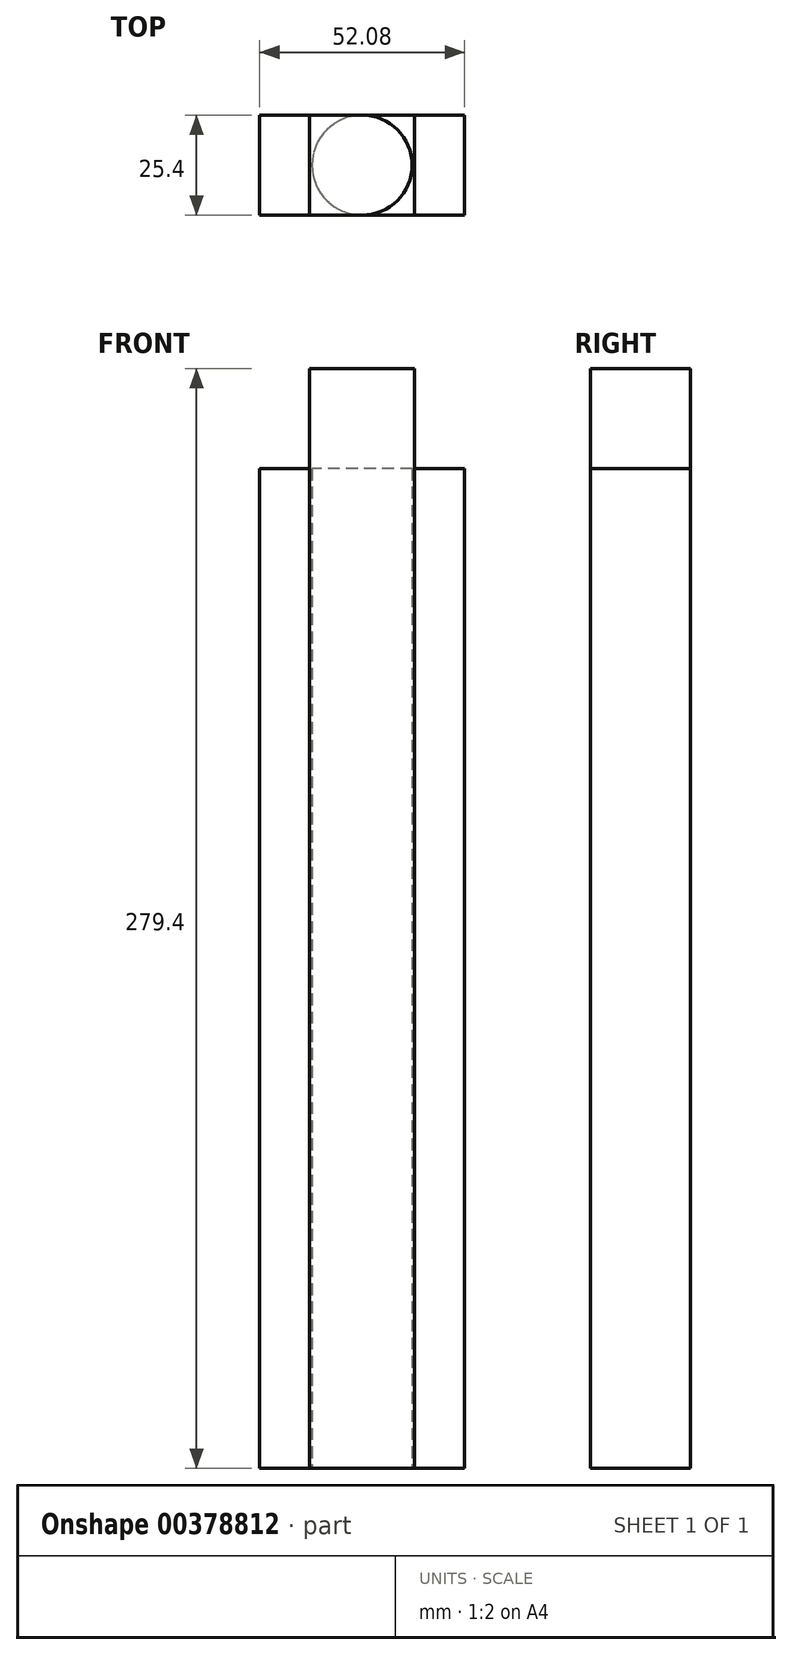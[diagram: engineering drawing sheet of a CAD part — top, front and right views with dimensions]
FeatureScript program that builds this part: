
annotation { "Feature Type Name" : "Feature", "Feature Type Description" : "" }
export const myFeature = defineFeature(function(context is Context, id is Id, definition is map)
    precondition{}
    {
        {
            var Q0;
            Q0=qCreatedBy(makeId("Top.planeOp"),FACE);
            var sketch = newSketch(context, id + "F0", { "sketchPlane" : qUnion([Q0])});
            skCircle(sketch, "E0", {"center": v(0, 0) * mm, "radius": 12.7 * mm});
            skSolve(sketch);
        }
        {
            var Q0;
            Q0=makeQuery(id+"F0.imprint","IMPRINT",FACE,{"disambiguationData":[TD([[makeQuery(id+"F0.imprint","IMPRINT",EDGE,{"derivedFrom":sQuery(id+"F0.wireOp",EDGE,"E0")}),1.0]])]});
            extrude(context, id + "F1", {"entities" : qUnion([Q0]), "depth" : 254 * mm});
        }
        {
            var Q0;
            Q0=qCreatedBy(makeId("Top.planeOp"),FACE);
            var sketch = newSketch(context, id + "F2", { "sketchPlane" : qUnion([Q0])});
            skLineSegment(sketch, "E1.bottom", {"start": v(9.53, -7.94) * mm, "end": v(-9.53, -7.94) * mm});
            skLineSegment(sketch, "E1.top", {"start": v(9.53, 7.94) * mm, "end": v(-9.53, 7.94) * mm});
            skLineSegment(sketch, "E1.left", {"start": v(9.53, -7.94) * mm, "end": v(9.53, 7.94) * mm});
            skLineSegment(sketch, "E1.right", {"start": v(-9.53, -7.94) * mm, "end": v(-9.53, 7.94) * mm});
            skPoint(sketch, "E1.middle", {"position": v(0, 0) * mm});
            skLineSegment(sketch, "E2.bottom", {"start": v(-13.33, 12.7) * mm, "end": v(13.34, 12.7) * mm});
            skLineSegment(sketch, "E2.top", {"start": v(-13.33, 3.18) * mm, "end": v(13.34, 3.18) * mm});
            skLineSegment(sketch, "E2.left", {"start": v(-13.33, 12.7) * mm, "end": v(-13.33, 3.18) * mm});
            skLineSegment(sketch, "E2.right", {"start": v(13.34, 12.7) * mm, "end": v(13.34, 3.18) * mm});
            skPoint(sketch, "E2.middle", {"position": v(0, 7.94) * mm});
            skLineSegment(sketch, "E3", {"start": v(-22.62, 0) * mm, "end": v(27.7, 0) * mm, "construction": true});
            skLineSegment(sketch, "E4.MirrorCS", {"start": v(-13.33, -12.7) * mm, "end": v(13.34, -12.7) * mm});
            skLineSegment(sketch, "E5.MirrorCS", {"start": v(-13.33, -12.7) * mm, "end": v(-13.33, -3.18) * mm});
            skLineSegment(sketch, "E6.MirrorCS", {"start": v(-13.33, -3.18) * mm, "end": v(13.34, -3.18) * mm});
            skLineSegment(sketch, "E7.MirrorCS", {"start": v(13.34, -12.7) * mm, "end": v(13.34, -3.18) * mm});
            skLineSegment(sketch, "E8.bottom", {"start": v(-13.33, 12.7) * mm, "end": v(-26.04, 12.7) * mm});
            skLineSegment(sketch, "E8.top", {"start": v(-13.33, -12.7) * mm, "end": v(-26.04, -12.7) * mm});
            skLineSegment(sketch, "E8.left", {"start": v(-13.33, 12.7) * mm, "end": v(-13.33, -12.7) * mm});
            skLineSegment(sketch, "E8.right", {"start": v(-26.04, 12.7) * mm, "end": v(-26.04, -12.7) * mm});
            skLineSegment(sketch, "E9.bottom", {"start": v(-9.52, -3.18) * mm, "end": v(-13.33, -3.18) * mm});
            skLineSegment(sketch, "E9.top", {"start": v(-9.52, 3.18) * mm, "end": v(-13.33, 3.18) * mm});
            skLineSegment(sketch, "E9.left", {"start": v(-9.53, -3.18) * mm, "end": v(-9.52, 3.18) * mm});
            skLineSegment(sketch, "E9.right", {"start": v(-13.33, -3.18) * mm, "end": v(-13.33, 3.18) * mm});
            skLineSegment(sketch, "E10", {"start": v(0, 20.94) * mm, "end": v(0, -20) * mm, "construction": true});
            skLineSegment(sketch, "E11.MirrorCS", {"start": v(13.33, -3.18) * mm, "end": v(13.33, 3.18) * mm});
            skLineSegment(sketch, "E12.MirrorCS", {"start": v(9.53, -3.18) * mm, "end": v(9.53, 3.18) * mm});
            skLineSegment(sketch, "E13.MirrorCS", {"start": v(13.33, -12.7) * mm, "end": v(13.33, -3.18) * mm});
            skLineSegment(sketch, "E14.MirrorCS", {"start": v(9.52, 3.18) * mm, "end": v(13.33, 3.18) * mm});
            skLineSegment(sketch, "E15.MirrorCS", {"start": v(13.33, -12.7) * mm, "end": v(26.04, -12.7) * mm});
            skLineSegment(sketch, "E16.MirrorCS", {"start": v(13.33, 12.7) * mm, "end": v(13.33, 3.18) * mm});
            skLineSegment(sketch, "E17.MirrorCS", {"start": v(13.33, 12.7) * mm, "end": v(26.04, 12.7) * mm});
            skLineSegment(sketch, "E18.MirrorCS", {"start": v(13.33, 12.7) * mm, "end": v(13.33, -12.7) * mm});
            skLineSegment(sketch, "E19.MirrorCS", {"start": v(9.52, -3.18) * mm, "end": v(13.33, -3.18) * mm});
            skLineSegment(sketch, "E20.MirrorCS", {"start": v(26.04, 12.7) * mm, "end": v(26.04, -12.7) * mm});
            skSolve(sketch);
        }
        {
            var Q0;
            {var subQ3=sQuery(id+"F2.wireOp",EDGE,"E8.bottom");Q0=makeQuery(id+"F2.imprint","IMPRINT",FACE,{"disambiguationData":[TD([[makeQuery(id+"F2.imprint","IMPRINT",EDGE,{"derivedFrom":subQ3}),1.0]])]});}
            var Q1;
            Q1=makeQuery(id+"F2.imprint","IMPRINT",FACE,{"disambiguationData":[TD([[makeQuery(id+"F2.imprint","IMPRINT",EDGE,{"derivedFrom":sQuery(id+"F2.wireOp",EDGE,"E9.bottom")}),-1.0]])]});
            var Q2;
            {var subQ0=sQuery(id+"F2.wireOp",EDGE,"E14.MirrorCS");Q2=makeQuery(id+"F2.imprint","IMPRINT",FACE,{"disambiguationData":[TD([[makeQuery(id+"F2.imprint","IMPRINT",EDGE,{"derivedFrom":subQ0}),-1.0]])]});}
            var Q3;
            {var subQ4=sQuery(id+"F2.wireOp",EDGE,"E15.MirrorCS");Q3=makeQuery(id+"F2.imprint","IMPRINT",FACE,{"disambiguationData":[TD([[makeQuery(id+"F2.imprint","IMPRINT",EDGE,{"derivedFrom":subQ4}),1.0]])]});}
            extrude(context, id + "F3", {"entities" : qUnion([Q0, Q1, Q2, Q3]), "depth" : 254 * mm});
        }
        {
            var Q0;
            {var subQ4=sQuery(id+"F2.wireOp",EDGE,"E1.top");Q0=makeQuery(id+"F2.imprint","IMPRINT",FACE,{"disambiguationData":[TD([[makeQuery(id+"F2.imprint","IMPRINT",EDGE,{"derivedFrom":subQ4}),-1.0]])]});}
            var Q1;
            {var subQ0=sQuery(id+"F2.wireOp",EDGE,"E1.top");Q1=makeQuery(id+"F2.imprint","IMPRINT",FACE,{"disambiguationData":[TD([[makeQuery(id+"F2.imprint","IMPRINT",EDGE,{"derivedFrom":subQ0}),1.0]])]});}
            var Q2;
            {var subQ0=sQuery(id+"F2.wireOp",EDGE,"E2.top");Q2=makeQuery(id+"F2.imprint","IMPRINT",FACE,{"disambiguationData":[TD([[makeQuery(id+"F2.imprint","IMPRINT",EDGE,{"derivedFrom":subQ0}),-1.0]])]});}
            var Q3;
            {var subQ0=sQuery(id+"F2.wireOp",EDGE,"E1.bottom");Q3=makeQuery(id+"F2.imprint","IMPRINT",FACE,{"disambiguationData":[TD([[makeQuery(id+"F2.imprint","IMPRINT",EDGE,{"derivedFrom":subQ0}),-1.0]])]});}
            var Q4;
            {var subQ3=sQuery(id+"F2.wireOp",EDGE,"E1.bottom");Q4=makeQuery(id+"F2.imprint","IMPRINT",FACE,{"disambiguationData":[TD([[makeQuery(id+"F2.imprint","IMPRINT",EDGE,{"derivedFrom":subQ3}),1.0]])]});}
            extrude(context, id + "F4", {"entities" : qUnion([Q0, Q1, Q2, Q3, Q4]), "depth" : 279.4 * mm});
        }
    });
